# Revit family: K-Form_K135_p_i_t_5021200
name_source: partatom
category: Generic Models
units: mm (PartAtom-declared; Revit-internal decimal feet)

## family parameters
Always vertical = No
Can host rebar = No
Cut with Voids When Loaded = No
Part Type = Normal
Room Calculation Point = No
Round Connector Dimension = Use Diameter
Shared = No
Work Plane-Based = Yes

## types (4) — shared parameters
Default Elevation = 1219 mm
Plastic = PVC

## per-type parameters (varying)
| type | K-Form Height | List Height | Yes/No Raiser |
| K-Form K85 w. Raiser | 85 mm | 114 mm | Yes |
| K-Form K135 | 135 mm  [stored 0.442913 ft] | 135 mm  [stored 0.442913 ft] | No |
| K-Form K85 | 85 mm | 85 mm | No |
| K-Form K135 w. Raiser | 135 mm  [stored 0.442913 ft] | 164 mm  [stored 0.538058 ft] | Yes |

note: [stored X ft] marks values corroborated as IEEE doubles in the binary element streams (Revit-internal decimal feet)

## geometry (parser evidence)
native form markers: Sweep x7
no freeform markers — native parametric forms only
